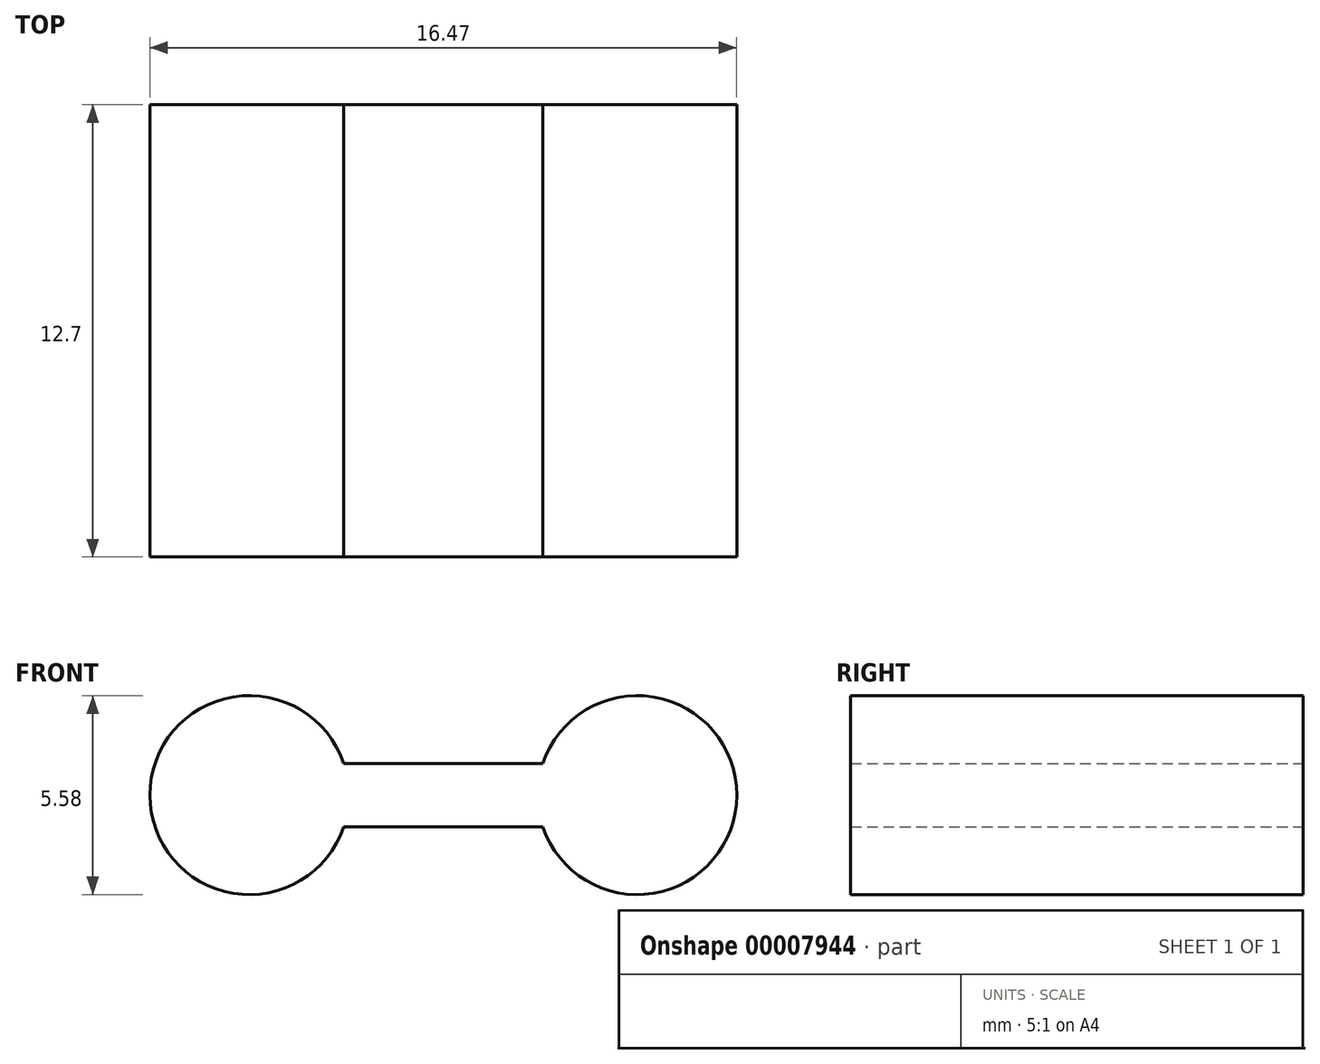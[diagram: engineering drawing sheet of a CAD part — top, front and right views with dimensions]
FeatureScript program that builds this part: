
annotation { "Feature Type Name" : "Feature", "Feature Type Description" : "" }
export const myFeature = defineFeature(function(context is Context, id is Id, definition is map)
    precondition{}
    {
        {
            var Q0;
            Q0=qCreatedBy(makeId("Front.planeOp"),FACE);
            var sketch = newSketch(context, id + "F0", { "sketchPlane" : qUnion([Q0])});
            skCircle(sketch, "E0", {"center": v(-22.25, 0) * mm, "radius": 2.8 * mm});
            skCircle(sketch, "E1", {"center": v(-11.37, 0) * mm, "radius": 2.8 * mm});
            skLineSegment(sketch, "E2", {"start": v(-19.6, 0.89) * mm, "end": v(-14.02, 0.89) * mm});
            skLineSegment(sketch, "E3", {"start": v(-19.6, -0.89) * mm, "end": v(-14.02, -0.89) * mm});
            skSolve(sketch);
        }
        {
            var Q0;
            Q0 = qSketchRegion(id + "F0", true);
            extrude(context, id + "F1", {"entities" : qUnion([Q0]), "depth" : 12.7 * mm});
        }
    });
